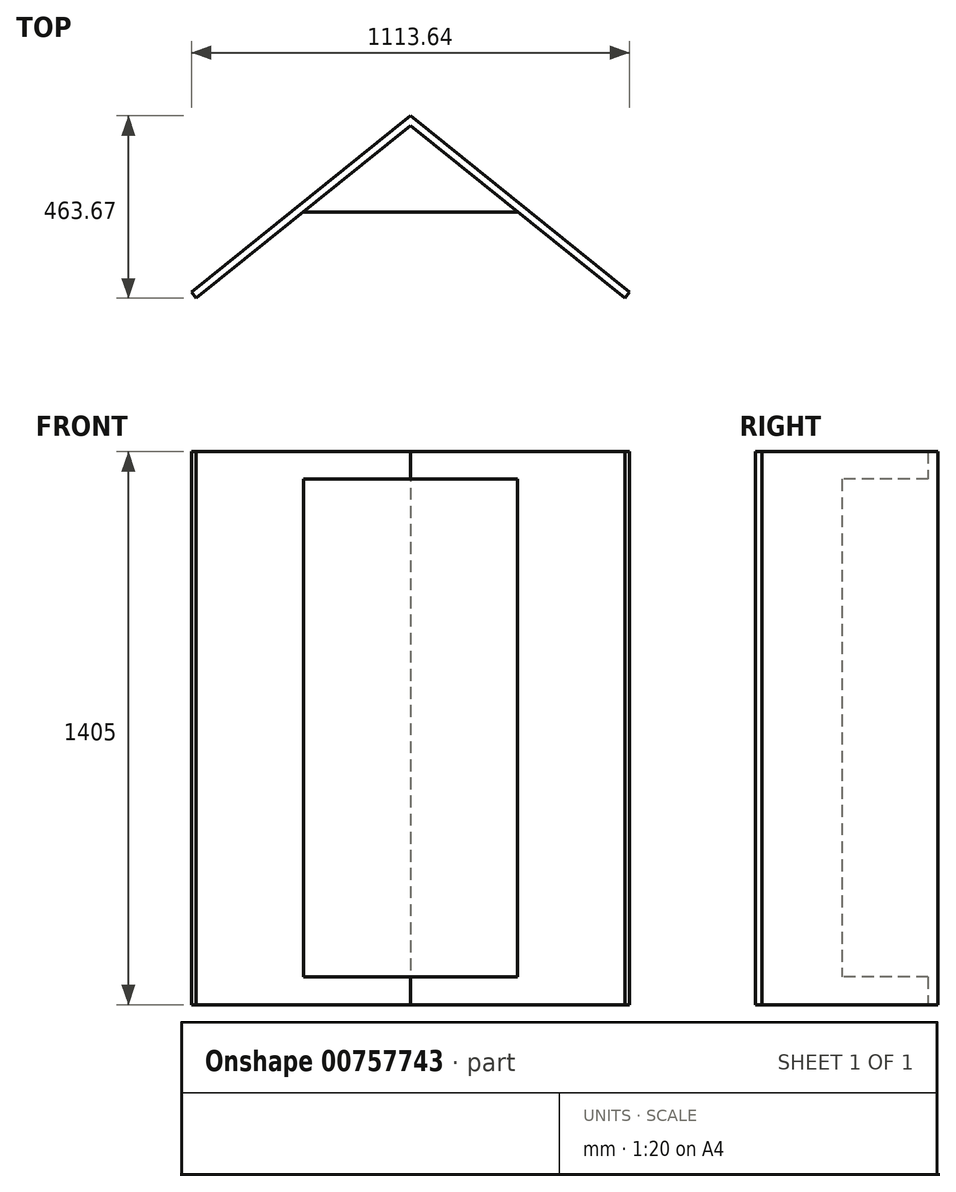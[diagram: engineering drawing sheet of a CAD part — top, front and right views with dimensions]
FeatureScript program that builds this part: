
annotation { "Feature Type Name" : "Feature", "Feature Type Description" : "" }
export const myFeature = defineFeature(function(context is Context, id is Id, definition is map)
    precondition{}
    {
        {
            var Q0;
            Q0=qCreatedBy(makeId("Top.planeOp"),FACE);
            var sketch = newSketch(context, id + "F0", { "sketchPlane" : qUnion([Q0])});
            skLineSegment(sketch, "E0", {"start": v(32.5, 30.44) * mm, "end": v(32.5, 249.44) * mm, "construction": true});
            skLineSegment(sketch, "E1", {"start": v(-390, -246.56) * mm, "end": v(-390, -90.56) * mm, "construction": true});
            skLineSegment(sketch, "E2", {"start": v(32.5, 249.44) * mm, "end": v(-390, -90.56) * mm});
            skLineSegment(sketch, "E3.MirrorCS", {"start": v(32.5, 249.44) * mm, "end": v(455, -90.56) * mm});
            skLineSegment(sketch, "E4", {"start": v(-390, -90.56) * mm, "end": v(-390, 249.44) * mm});
            skLineSegment(sketch, "E5", {"start": v(-390, 249.44) * mm, "end": v(455, 249.44) * mm});
            skLineSegment(sketch, "E6", {"start": v(455, 249.44) * mm, "end": v(455, -90.56) * mm});
            skLineSegment(sketch, "E7", {"start": v(455, -90.56) * mm, "end": v(576.78, -188.56) * mm});
            skLineSegment(sketch, "E8", {"start": v(576.78, -188.56) * mm, "end": v(589.32, -172.98) * mm});
            skLineSegment(sketch, "E9", {"start": v(589.32, -172.98) * mm, "end": v(32.5, 275.1) * mm});
            skLineSegment(sketch, "E10.MirrorCS", {"start": v(-524.32, -172.98) * mm, "end": v(32.5, 275.1) * mm});
            skLineSegment(sketch, "E11.MirrorCS", {"start": v(-390, -90.56) * mm, "end": v(-511.78, -188.56) * mm});
            skLineSegment(sketch, "E12.MirrorCS", {"start": v(-511.78, -188.56) * mm, "end": v(-524.32, -172.98) * mm});
            skLineSegment(sketch, "E13", {"start": v(32.5, 30.44) * mm, "end": v(-239.64, 30.44) * mm});
            skLineSegment(sketch, "E14.MirrorCS", {"start": v(32.5, 30.44) * mm, "end": v(304.64, 30.44) * mm});
            skLineSegment(sketch, "E15.0", {"start": v(32.5, 35.44) * mm, "end": v(-239.64, 35.44) * mm});
            skLineSegment(sketch, "E15.1", {"start": v(32.5, 35.44) * mm, "end": v(304.64, 35.44) * mm});
            skSolve(sketch);
        }
        {
            var Q0;
            {var subQ0=sQuery(id+"F0.wireOp",EDGE,"E11.MirrorCS");Q0=makeQuery(id+"F0.imprint","IMPRINT",FACE,{"disambiguationData":[TD([[makeQuery(id+"F0.imprint","IMPRINT",EDGE,{"derivedFrom":subQ0}),-1.0]])]});}
            var Q1;
            {var subQ0=sQuery(id+"F0.wireOp",EDGE,"E2");Q1=makeQuery(id+"F0.imprint","IMPRINT",FACE,{"disambiguationData":[TD([[makeQuery(id+"F0.imprint","IMPRINT",EDGE,{"derivedFrom":subQ0}),-1.0]])]});}
            var Q2;
            {var subQ2=sQuery(id+"F0.wireOp",EDGE,"E10.MirrorCS");var subQ4=sQuery(id+"F0.wireOp",EDGE,"E9");var subQ6=makeQuery(id+"F0.imprint","INTERSECT",VERTEX,{"derivedFrom":[subQ4,subQ2]});Q2=makeQuery(id+"F0.imprint","IMPRINT",FACE,{"disambiguationData":[TD([[makeQuery(id+"F0.imprint","IMPRINT",EDGE,{"disambiguationData":[TD([[subQ6,1.0]])],"derivedFrom":subQ4}),1.0]])]});}
            var Q3;
            {var subQ0=sQuery(id+"F0.wireOp",EDGE,"E3.MirrorCS");Q3=makeQuery(id+"F0.imprint","IMPRINT",FACE,{"disambiguationData":[TD([[makeQuery(id+"F0.imprint","IMPRINT",EDGE,{"derivedFrom":subQ0}),1.0]])]});}
            var Q4;
            {var subQ0=sQuery(id+"F0.wireOp",EDGE,"E7");Q4=makeQuery(id+"F0.imprint","IMPRINT",FACE,{"disambiguationData":[TD([[makeQuery(id+"F0.imprint","IMPRINT",EDGE,{"derivedFrom":subQ0}),1.0]])]});}
            extrude(context, id + "F1", {"entities" : qUnion([Q0, Q1, Q2, Q3, Q4]), "depth" : 1335 * mm, "offsetDistance" : 25 * mm, "hasSecondDirection" : true, "secondDirectionOppositeDirection" : true, "secondDirectionDepth" : 70 * mm});
        }
        {
            var Q0;
            {var subQ3=sQuery(id+"F0.wireOp",EDGE,"E15.0");var subQ5=sQuery(id+"F0.wireOp",EDGE,"E15.1");var subQ7=makeQuery(id+"F0.imprint","INTERSECT",VERTEX,{"derivedFrom":[subQ3,subQ5]});Q0=makeQuery(id+"F0.imprint","IMPRINT",FACE,{"disambiguationData":[TD([[makeQuery(id+"F0.imprint","IMPRINT",EDGE,{"disambiguationData":[TD([[subQ7,-1.0]])],"derivedFrom":subQ3}),-1.0]])]});}
            var Q1;
            {var subQ1=sQuery(id+"F0.wireOp",EDGE,"E13");Q1=makeQuery(id+"F0.imprint","IMPRINT",FACE,{"disambiguationData":[TD([[makeQuery(id+"F0.imprint","IMPRINT",EDGE,{"derivedFrom":subQ1}),-1.0]])]});}
            extrude(context, id + "F2", {"entities" : qUnion([Q0, Q1]), "operationType" : NewBodyOperationType.ADD, "depth" : (1335 - 70) * mm, "offsetDistance" : 25 * mm});
        }
    });
